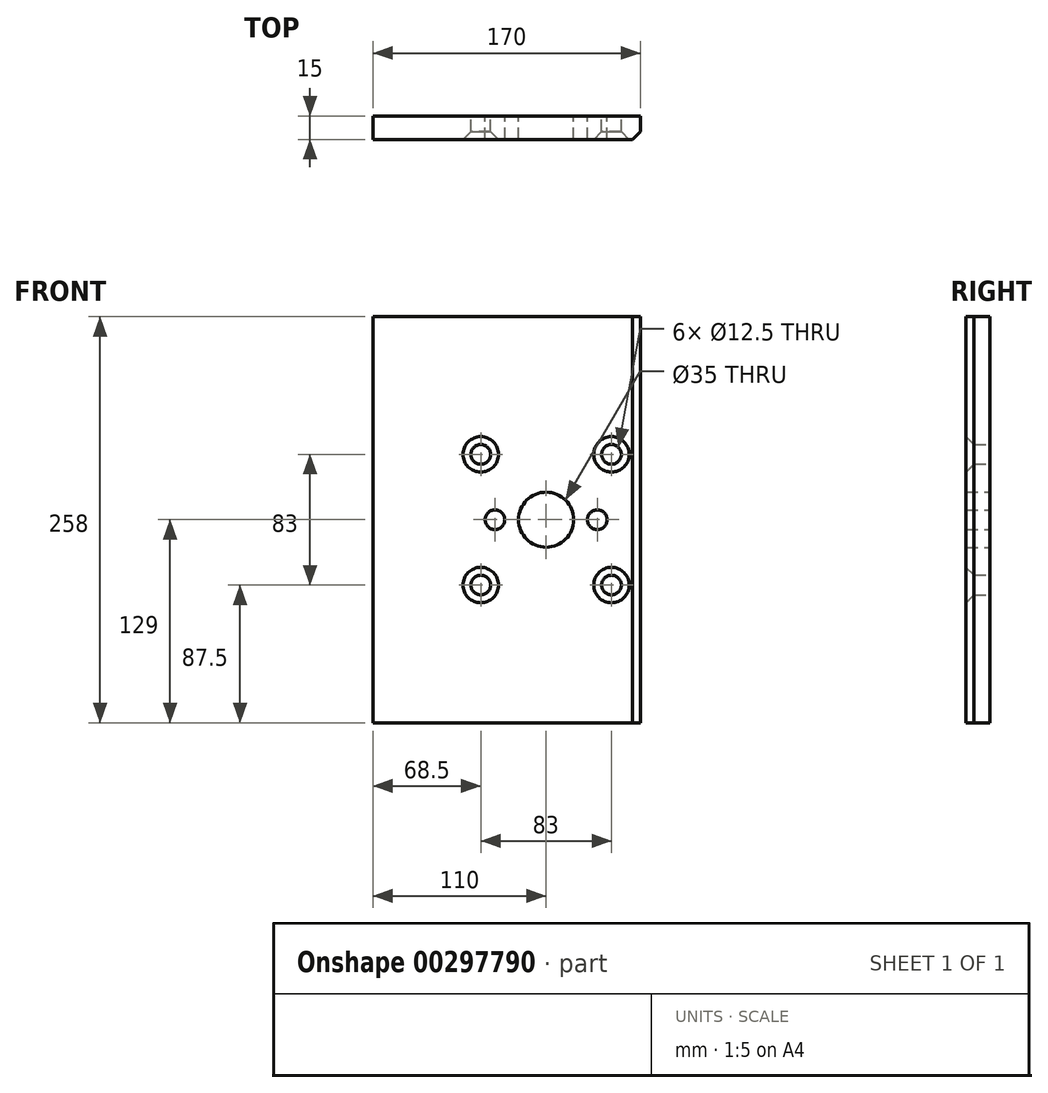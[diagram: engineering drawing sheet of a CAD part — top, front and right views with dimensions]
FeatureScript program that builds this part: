
annotation { "Feature Type Name" : "Feature", "Feature Type Description" : "" }
export const myFeature = defineFeature(function(context is Context, id is Id, definition is map)
    precondition{}
    {
        {
            var Q0;
            Q0=qCreatedBy(makeId("Front.planeOp"),FACE);
            var sketch = newSketch(context, id + "F0", { "sketchPlane" : qUnion([Q0])});
            skLineSegment(sketch, "E0.bottom", {"start": v(60, 129) * mm, "end": v(-110, 129) * mm});
            skLineSegment(sketch, "E0.top", {"start": v(60, -129) * mm, "end": v(-110, -129) * mm});
            skLineSegment(sketch, "E0.left", {"start": v(60, 129) * mm, "end": v(60, -129) * mm});
            skLineSegment(sketch, "E0.right", {"start": v(-110, 129) * mm, "end": v(-110, -129) * mm});
            skPoint(sketch, "E0.middle", {"position": v(0, 0) * mm});
            skCircle(sketch, "E1", {"center": v(0, 0) * mm, "radius": 17.5 * mm});
            skCircle(sketch, "E2", {"center": v(0, 0) * mm, "radius": 32.5 * mm, "construction": true});
            skCircle(sketch, "E3", {"center": v(-32.5, 0) * mm, "radius": 6.25 * mm});
            skCircle(sketch, "E4", {"center": v(32.5, 0) * mm, "radius": 6.25 * mm});
            skLineSegment(sketch, "E5.bottom", {"start": v(41.5, 41.5) * mm, "end": v(-41.5, 41.5) * mm, "construction": true});
            skLineSegment(sketch, "E5.top", {"start": v(41.5, -41.5) * mm, "end": v(-41.5, -41.5) * mm, "construction": true});
            skLineSegment(sketch, "E5.left", {"start": v(41.5, 41.5) * mm, "end": v(41.5, -41.5) * mm, "construction": true});
            skLineSegment(sketch, "E5.right", {"start": v(-41.5, 41.5) * mm, "end": v(-41.5, -41.5) * mm, "construction": true});
            skCircle(sketch, "E6", {"center": v(-41.5, 41.5) * mm, "radius": 6.25 * mm});
            skCircle(sketch, "E7", {"center": v(41.5, 41.5) * mm, "radius": 6.25 * mm});
            skCircle(sketch, "E8", {"center": v(41.5, -41.5) * mm, "radius": 6.25 * mm});
            skCircle(sketch, "E9", {"center": v(-41.5, -41.5) * mm, "radius": 6.25 * mm});
            skSolve(sketch);
        }
        {
            var Q0;
            Q0 = qSketchRegion(id + "F0", true);
            extrude(context, id + "F1", {"entities" : qUnion([Q0]), "depth" : 15 * mm});
        }
        {
            var Q0;
            Q0=makeQuery(id+"F1.opExtrude","CAP_EDGE",EDGE,{"disambiguationData":[OSD([sQuery(id+"F0.wireOp",EDGE,"E6")])],"isStart":false});
            var Q1;
            Q1=makeQuery(id+"F1.opExtrude","CAP_EDGE",EDGE,{"disambiguationData":[OSD([sQuery(id+"F0.wireOp",EDGE,"E7")])],"isStart":false});
            var Q2;
            Q2=makeQuery(id+"F1.opExtrude","CAP_EDGE",EDGE,{"disambiguationData":[OSD([sQuery(id+"F0.wireOp",EDGE,"E9")])],"isStart":false});
            var Q3;
            Q3=makeQuery(id+"F1.opExtrude","CAP_EDGE",EDGE,{"disambiguationData":[OSD([sQuery(id+"F0.wireOp",EDGE,"E8")])],"isStart":false});
            var Q4;
            Q4=makeQuery(id+"F1.opExtrude","CAP_EDGE",EDGE,{"disambiguationData":[OSD([sQuery(id+"F0.wireOp",EDGE,"E0.left")])],"isStart":false});
            chamfer(context, id + "F2", {"entities" : qUnion([Q0, Q1, Q2, Q3, Q4]), "chamferType" : ChamferType.OFFSET_ANGLE, "width" : 5 * mm, "oppositeDirection" : false, "angle" : 45 * degree, "tangentPropagation" : true});
        }
    });
